FCSTD DOCUMENT  (FreeCAD 0.20R29410 (Git))
Label: #0_ASSEMBLY
License: All rights reserved
LicenseURL: http://en.wikipedia.org/wiki/All_rights_reserved
objects: Part::FeaturePython×22, App::FeaturePython×20
note: 22 computed .brp shape members not serialized (recipe doc carries the construction recipe); baked Part::Feature solids carry a one-line shape summary decoded from their .brp

FEATURE [Part::FeaturePython] b__0_ASSEMBLY_MAIN_BASE_001_  label="#0_ASSEMBLY_MAIN_BASE_001"  # a2plus imported part (geometry in sourceFile) (typed FeaturePython)
  a2p_Version = 0.4.60k
  fixedPosition = true
  objectType = a2pPart
  sourceFile = .\#0_ASSEMBLY_MAIN_BASE.FCStd
  subassemblyImport = true
  timeLastImport = 1.68898e+09
  updateColors = true
FEATURE [Part::FeaturePython] b__0_ASSEMBLY_MOTORS_BASE_001_  label="#0_ASSEMBLY_MOTORS_BASE_001"  # a2plus imported part (geometry in sourceFile) (typed FeaturePython)
  Placement = pos=(-1.19586e-08,4.9361e-09,78) rot=(0,0,1;0.440187rad)
  a2p_Version = 0.4.60k
  fixedPosition = false
  objectType = a2pPart
  sourceFile = .\#0_ASSEMBLY_MOTORS_BASE.FCStd
  subassemblyImport = false
  timeLastImport = 1.68866e+09
  updateColors = true
FEATURE [App::FeaturePython] circularEdge_001  label="circularEdge_001__#0_ASSEMBLY_MAIN_BASE_001"  # a2plus constraint (typed FeaturePython)
  Object1 = b__0_ASSEMBLY_MOTORS_BASE_001_
  Object2 = b__0_ASSEMBLY_MAIN_BASE_001_
  ParentTreeObject = -> b__0_ASSEMBLY_MOTORS_BASE_001_
  SubElement1 = Edge7445
  SubElement2 = Edge19302
  Suppressed = false
  Type = circularEdge
  directionConstraint = 1
  lockRotation = false
  offset = 0
FEATURE [App::FeaturePython] circularEdge_001_mirror  label="circularEdge_001__#0_ASSEMBLY_MOTORS_BASE_001"  # a2plus constraint (typed FeaturePython)
  Object1 = b__0_ASSEMBLY_MOTORS_BASE_001_
  Object2 = b__0_ASSEMBLY_MAIN_BASE_001_
  ParentTreeObject = -> b__0_ASSEMBLY_MAIN_BASE_001_
  SubElement1 = Edge7445
  SubElement2 = Edge19302
  Suppressed = false
  Type = circularEdge
  directionConstraint = 1
  lockRotation = false
  offset = 0
FEATURE [Part::FeaturePython] b__0_ASSEMBLY_LINKS_001_  label="#0_ASSEMBLY_LINKS_001"  # a2plus imported part (geometry in sourceFile) (typed FeaturePython)
  Placement = pos=(14.0996,-32.047,132) rot=(0.696251,0.162561,0.699148;3.43862rad)
  a2p_Version = 0.4.60k
  fixedPosition = false
  objectType = a2pPart
  sourceFile = .\#0_ASSEMBLY_LINKS.FCStd
  subassemblyImport = false
  timeLastImport = 1.6896e+09
  updateColors = true
FEATURE [Part::FeaturePython] ThreadedRod  label="M5x102-Barra roscada"  # Fasteners workbench fastener (typed FeaturePython)
  Placement = pos=(-31.4316,-53.3188,132.053) rot=(0.42611,-0.904671,0;1.57174rad)
  baseObject = -> b__0_ASSEMBLY_MOTORS_BASE_001_ [Edge13899]
  diameter = 7
  diameterCustom = 102
  invert = false
  leftHanded = false
  length = 102
  matchOuter = false
  offset = 6
  pitchCustom = 1
  thread = false
  type = 4
FEATURE [Part::FeaturePython] Nut  label="M5-Tuerca"  # Fasteners workbench fastener (typed FeaturePython)
  Placement = pos=(-26.0036,-50.7622,132.059) rot=(0.42611,-0.904671,0;1.57174rad)
  baseObject = -> b__0_ASSEMBLY_MOTORS_BASE_001_ [Edge14007]
  diameter = 3
  invert = false
  leftHanded = false
  matchOuter = false
  offset = 0
  thread = false
  type = 19
FEATURE [Part::FeaturePython] Nut001  label="M5-Tuerca001"  # Fasteners workbench fastener (typed FeaturePython)
  Placement = pos=(55.5978,-12.3271,132.144) rot=(-0.42611,0.904671,0;1.56985rad)
  baseObject = -> b__0_ASSEMBLY_MOTORS_BASE_001_ [Edge2058]
  diameter = 3
  invert = true
  leftHanded = false
  matchOuter = false
  offset = 0
  thread = false
  type = 19
FEATURE [Part::FeaturePython] b__0_ASSEMBLY_END_EFFECTOR_001_  label="#0_ASSEMBLY_END_EFFECTOR_001"  # a2plus imported part (geometry in sourceFile) (typed FeaturePython)
  Placement = pos=(110.856,-155.333,234.22) rot=(0.740663,-0.487527,-0.462316;1.8461rad)
  a2p_Version = 0.4.60k
  fixedPosition = false
  objectType = a2pPart
  sourceFile = .\#0_ASSEMBLY_END_EFFECTOR.FCStd
  subassemblyImport = true
  timeLastImport = 1.68901e+09
  updateColors = true
FEATURE [Part::FeaturePython] Washer  label="M5-Arandela"  # Fasteners workbench fastener (typed FeaturePython)
  Placement = pos=(77.3836,-171.099,234.22) rot=(0.738282,-0.496799,-0.456212;1.83675rad)
  diameter = 6
  invert = false
  matchOuter = false
  offset = 0
  type = 4
FEATURE [App::FeaturePython] circularEdge_003  label="circularEdge_003__#0_ASSEMBLY_LINKS_001"  # a2plus constraint (typed FeaturePython)
  Object1 = Washer
  Object2 = b__0_ASSEMBLY_LINKS_001_
  ParentTreeObject = -> Washer
  SubElement1 = Edge1
  SubElement2 = Edge30660
  Suppressed = false
  Type = circularEdge
  directionConstraint = 0
  lockRotation = false
  offset = 0
FEATURE [App::FeaturePython] circularEdge_003_mirror  label="circularEdge_003__M5-Arandela"  # a2plus constraint (typed FeaturePython)
  Object1 = Washer
  Object2 = b__0_ASSEMBLY_LINKS_001_
  ParentTreeObject = -> b__0_ASSEMBLY_LINKS_001_
  SubElement1 = Edge1
  SubElement2 = Edge30660
  Suppressed = false
  Type = circularEdge
  directionConstraint = 0
  lockRotation = false
  offset = 0
FEATURE [Part::FeaturePython] Washer001  label="M5-Arandela027"  # Fasteners workbench fastener (typed FeaturePython)
  Placement = pos=(123.852,-180.578,254.708) rot=(0.246024,0.791298,0.55975;2.04461rad)
  diameter = 6
  invert = false
  matchOuter = false
  offset = 0
  type = 4
FEATURE [Part::FeaturePython] Washer002  label="M5-Arandela028"  # Fasteners workbench fastener (typed FeaturePython)
  Placement = pos=(78.2882,-170.672,234.22) rot=(-0.655508,-0.266534,0.70659;3.21794rad)
  diameter = 6
  invert = false
  matchOuter = false
  offset = 0
  type = 4
FEATURE [App::FeaturePython] circularEdge_004  label="circularEdge_004__#0_ASSEMBLY_LINKS_001"  # a2plus constraint (typed FeaturePython)
  Object1 = Washer001
  Object2 = b__0_ASSEMBLY_LINKS_001_
  ParentTreeObject = -> Washer001
  SubElement1 = Edge1
  SubElement2 = Edge31281
  Suppressed = false
  Type = circularEdge
  directionConstraint = 1
  lockRotation = false
  offset = 0
FEATURE [App::FeaturePython] circularEdge_004_mirror  label="circularEdge_004__M5-Arandela003"  # a2plus constraint (typed FeaturePython)
  Object1 = Washer001
  Object2 = b__0_ASSEMBLY_LINKS_001_
  ParentTreeObject = -> b__0_ASSEMBLY_LINKS_001_
  SubElement1 = Edge1
  SubElement2 = Edge31281
  Suppressed = false
  Type = circularEdge
  directionConstraint = 1
  lockRotation = false
  offset = 0
FEATURE [App::FeaturePython] circularEdge_005  label="circularEdge_005__M5-Arandela003"  # a2plus constraint (typed FeaturePython)
  Object1 = b__0_ASSEMBLY_END_EFFECTOR_001_
  Object2 = Washer001
  ParentTreeObject = -> b__0_ASSEMBLY_END_EFFECTOR_001_
  SubElement1 = Edge173
  SubElement2 = Edge3
  Suppressed = false
  Type = circularEdge
  directionConstraint = 0
  lockRotation = false
  offset = 0
FEATURE [App::FeaturePython] circularEdge_005_mirror  label="circularEdge_005__#0_ASSEMBLY_END_EFFECTOR_001"  # a2plus constraint (typed FeaturePython)
  Object1 = b__0_ASSEMBLY_END_EFFECTOR_001_
  Object2 = Washer001
  ParentTreeObject = -> Washer001
  SubElement1 = Edge173
  SubElement2 = Edge3
  Suppressed = false
  Type = circularEdge
  directionConstraint = 0
  lockRotation = false
  offset = 0
FEATURE [App::FeaturePython] circularEdge_006  label="circularEdge_006__M5-Arandela"  # a2plus constraint (typed FeaturePython)
  Object1 = Washer002
  Object2 = Washer
  ParentTreeObject = -> Washer002
  SubElement1 = Edge1
  SubElement2 = Edge3
  Suppressed = false
  Type = circularEdge
  directionConstraint = 0
  lockRotation = false
  offset = 0
FEATURE [App::FeaturePython] circularEdge_006_mirror  label="circularEdge_006__M5-Arandela004"  # a2plus constraint (typed FeaturePython)
  Object1 = Washer002
  Object2 = Washer
  ParentTreeObject = -> Washer
  SubElement1 = Edge1
  SubElement2 = Edge3
  Suppressed = false
  Type = circularEdge
  directionConstraint = 0
  lockRotation = false
  offset = 0
FEATURE [App::FeaturePython] circularEdge_007  label="circularEdge_007__#0_ASSEMBLY_END_EFFECTOR_001"  # a2plus constraint (typed FeaturePython)
  Object1 = Washer002
  Object2 = b__0_ASSEMBLY_END_EFFECTOR_001_
  ParentTreeObject = -> Washer002
  SubElement1 = Edge3
  SubElement2 = Edge131
  Suppressed = false
  Type = circularEdge
  directionConstraint = 0
  lockRotation = false
  offset = 0
FEATURE [App::FeaturePython] circularEdge_007_mirror  label="circularEdge_007__M5-Arandela008"  # a2plus constraint (typed FeaturePython)
  Object1 = Washer002
  Object2 = b__0_ASSEMBLY_END_EFFECTOR_001_
  ParentTreeObject = -> b__0_ASSEMBLY_END_EFFECTOR_001_
  SubElement1 = Edge3
  SubElement2 = Edge131
  Suppressed = false
  Type = circularEdge
  directionConstraint = 0
  lockRotation = false
  offset = 0
FEATURE [Part::FeaturePython] Screw  label="M5x60-Tornillo"  # Fasteners workbench fastener (typed FeaturePython)
  Placement = pos=(62.9088,-177.916,234.22) rot=(0.426109,-0.904672,0;1.5708rad)
  baseObject = -> b__0_ASSEMBLY_LINKS_001_ [Edge30684]
  diameter = 6
  invert = false
  leftHanded = false
  length = 12
  lengthCustom = 60
  matchOuter = false
  offset = 0
  thread = false
  type = 45
FEATURE [Part::FeaturePython] Nut002  label="M5-Tuerca006"  # Fasteners workbench fastener (typed FeaturePython)
  Placement = pos=(111.761,-154.906,234.22) rot=(-0.42611,0.904672,0;1.57079rad)
  baseObject = -> b__0_ASSEMBLY_END_EFFECTOR_001_ [Edge150]
  diameter = 3
  invert = false
  leftHanded = false
  matchOuter = false
  offset = 0
  thread = false
  type = 19
FEATURE [Part::FeaturePython] Screw002  label="M4x30-Tornillo"  # Fasteners workbench fastener (typed FeaturePython)
  Placement = pos=(101.103,-175.694,242.205) rot=(-0.904644,-0.426167,0;0.033672rad)
  baseObject = -> b__0_ASSEMBLY_END_EFFECTOR_001_ [Edge56]
  diameter = 5
  invert = true
  leftHanded = false
  length = 8
  lengthCustom = 30
  matchOuter = false
  offset = 0
  thread = false
  type = 45
FEATURE [Part::FeaturePython] b__23_TOOL_Electromagnet_001_  label="#23_TOOL_Electromagnet_001"  # a2plus imported part (geometry in sourceFile) (typed FeaturePython)
  Placement = pos=(107.692,-156.829,234.22) rot=(-0.016828,-0.026531,-0.999506;1.13105rad)
  a2p_Version = 0.4.60k
  fixedPosition = false
  objectType = a2pPart
  sourceFile = .\#23_TOOL_Electromagnet.FCStd
  subassemblyImport = false
  timeLastImport = 1.68901e+09
  updateColors = true
FEATURE [App::FeaturePython] circularEdge_008  label="circularEdge_008__#0_ASSEMBLY_END_EFFECTOR_001"  # a2plus constraint (typed FeaturePython)
  Object1 = b__23_TOOL_Electromagnet_001_
  Object2 = b__0_ASSEMBLY_END_EFFECTOR_001_
  ParentTreeObject = -> b__23_TOOL_Electromagnet_001_
  SubElement1 = Edge23
  SubElement2 = Edge45
  Suppressed = false
  Type = circularEdge
  directionConstraint = 0
  lockRotation = false
  offset = 0
FEATURE [App::FeaturePython] circularEdge_008_mirror  label="circularEdge_008__#23_TOOL_Electromagnet_001"  # a2plus constraint (typed FeaturePython)
  Object1 = b__23_TOOL_Electromagnet_001_
  Object2 = b__0_ASSEMBLY_END_EFFECTOR_001_
  ParentTreeObject = -> b__0_ASSEMBLY_END_EFFECTOR_001_
  SubElement1 = Edge23
  SubElement2 = Edge45
  Suppressed = false
  Type = circularEdge
  directionConstraint = 0
  lockRotation = false
  offset = 0
FEATURE [App::FeaturePython] planesParallel_001  label="planesParallel_001__#0_ASSEMBLY_END_EFFECTOR_001"  # a2plus constraint (typed FeaturePython)
  Object1 = b__23_TOOL_Electromagnet_001_
  Object2 = b__0_ASSEMBLY_END_EFFECTOR_001_
  ParentTreeObject = -> b__23_TOOL_Electromagnet_001_
  SubElement1 = Face8
  SubElement2 = Face15
  Suppressed = false
  Type = planesParallel
  directionConstraint = 1
FEATURE [App::FeaturePython] planesParallel_001_mirror  label="planesParallel_001__#23_TOOL_Electromagnet_001"  # a2plus constraint (typed FeaturePython)
  Object1 = b__23_TOOL_Electromagnet_001_
  Object2 = b__0_ASSEMBLY_END_EFFECTOR_001_
  ParentTreeObject = -> b__0_ASSEMBLY_END_EFFECTOR_001_
  SubElement1 = Face8
  SubElement2 = Face15
  Suppressed = false
  Type = planesParallel
  directionConstraint = 1
FEATURE [Part::FeaturePython] b_electromagnet1_001_  label="electromagnet1_001"  # a2plus imported part (geometry in sourceFile) (typed FeaturePython)
  Placement = pos=(113.118,-148.837,207.54) rot=(0.844341,-0.535618,0.014217;3.12356rad)
  a2p_Version = 0.4.60k
  fixedPosition = false
  objectType = a2pPart
  sourceFile = .\..\Complements\electromagnet.step
  subassemblyImport = false
  timeLastImport = 1.68866e+09
  updateColors = true
FEATURE [App::FeaturePython] circularEdge_009  label="circularEdge_009__#23_TOOL_Electromagnet_001"  # a2plus constraint (typed FeaturePython)
  Object1 = b_electromagnet1_001_
  Object2 = b__23_TOOL_Electromagnet_001_
  ParentTreeObject = -> b_electromagnet1_001_
  SubElement1 = Edge101
  SubElement2 = Edge31
  Suppressed = false
  Type = circularEdge
  directionConstraint = 0
  lockRotation = false
  offset = 0
FEATURE [App::FeaturePython] circularEdge_009_mirror  label="circularEdge_009__electromagnet1_001"  # a2plus constraint (typed FeaturePython)
  Object1 = b_electromagnet1_001_
  Object2 = b__23_TOOL_Electromagnet_001_
  ParentTreeObject = -> b__23_TOOL_Electromagnet_001_
  SubElement1 = Edge101
  SubElement2 = Edge31
  Suppressed = false
  Type = circularEdge
  directionConstraint = 0
  lockRotation = false
  offset = 0
FEATURE [App::FeaturePython] axisParallel_001  label="axisParallel_001__#0_ASSEMBLY_END_EFFECTOR_001"  # a2plus constraint (typed FeaturePython)
  Object1 = b_electromagnet1_001_
  Object2 = b__0_ASSEMBLY_END_EFFECTOR_001_
  ParentTreeObject = -> b_electromagnet1_001_
  SubElement1 = Edge509
  SubElement2 = Edge39
  Suppressed = false
  Type = axisParallel
  directionConstraint = 1
FEATURE [App::FeaturePython] axisParallel_001_mirror  label="axisParallel_001__electromagnet1_001"  # a2plus constraint (typed FeaturePython)
  Object1 = b_electromagnet1_001_
  Object2 = b__0_ASSEMBLY_END_EFFECTOR_001_
  ParentTreeObject = -> b__0_ASSEMBLY_END_EFFECTOR_001_
  SubElement1 = Edge509
  SubElement2 = Edge39
  Suppressed = false
  Type = axisParallel
  directionConstraint = 1
FEATURE [Part::FeaturePython] Screw003  label="M5x55-Tornillo"  # Fasteners workbench fastener (typed FeaturePython)
  Placement = pos=(90.3797,-196.344,254.708) rot=(0.426109,-0.904672,0;1.5708rad)
  baseObject = -> b__0_ASSEMBLY_END_EFFECTOR_001_ [Edge198]
  diameter = 6
  invert = true
  leftHanded = false
  length = 12
  lengthCustom = 55
  matchOuter = false
  offset = 0
  thread = false
  type = 45
FEATURE [Part::FeaturePython] Nut003  label="M5-Tuerca003"  # Fasteners workbench fastener (typed FeaturePython)
  Placement = pos=(133.804,-175.891,254.708) rot=(-0.426108,0.904672,0;1.5708rad)
  baseObject = -> b__0_ASSEMBLY_LINKS_001_ [Edge31240]
  diameter = 3
  invert = true
  leftHanded = false
  matchOuter = false
  offset = 0
  thread = false
  type = 19
FEATURE [Part::FeaturePython] Screw004  label="M5x50-Tornillo"  # Fasteners workbench fastener (typed FeaturePython)
  Placement = pos=(-1.5558e-07,1.49855e-07,90) rot=(0,0,1;0rad)
  baseObject = -> b__0_ASSEMBLY_MOTORS_BASE_001_ [Edge10606]
  diameter = 6
  invert = false
  leftHanded = false
  length = 12
  lengthCustom = 50
  matchOuter = false
  offset = 0
  thread = false
  type = 45
FEATURE [Part::FeaturePython] Nut004  label="M5-Tuerca004"  # Fasteners workbench fastener (typed FeaturePython)
  Placement = pos=(5.78876e-09,3.54658e-09,46) rot=(0.879202,-0.47645,0;3.14159rad)
  baseObject = -> b__0_ASSEMBLY_MAIN_BASE_001_ [Edge1000]
  diameter = 3
  invert = false
  leftHanded = false
  matchOuter = false
  offset = 0
  thread = false
  type = 19
FEATURE [Part::FeaturePython] Screw005  label="M4x30-Tornillo001"  # Fasteners workbench fastener (typed FeaturePython)
  Placement = pos=(101,-175.4,242.2) rot=(0,0,1;0rad)
  diameter = 5
  invert = false
  leftHanded = false
  length = 11
  lengthCustom = 30
  matchOuter = false
  offset = 0
  thread = true
  type = 45
FEATURE [Part::FeaturePython] Screw006  label="M5x30-Tornillo"  # Fasteners workbench fastener (typed FeaturePython)
  Placement = pos=(54.0327,21.6351,156.59) rot=(-0.426109,0.904672,0;1.57079rad)
  baseObject = -> b__0_ASSEMBLY_LINKS_001_ [Edge30867]
  diameter = 6
  invert = false
  leftHanded = false
  length = 7
  lengthCustom = 30
  matchOuter = false
  offset = 0
  thread = false
  type = 45
FEATURE [Part::FeaturePython] Nut005  label="M5-Tuerca005"  # Fasteners workbench fastener (typed FeaturePython)
  Placement = pos=(33.6111,11.0137,157.712) rot=(0.426109,-0.904672,0;1.5708rad)
  baseObject = -> b__0_ASSEMBLY_MOTORS_BASE_001_ [Edge3242]
  diameter = 3
  invert = false
  leftHanded = false
  matchOuter = false
  offset = 0
  thread = false
  type = 19
